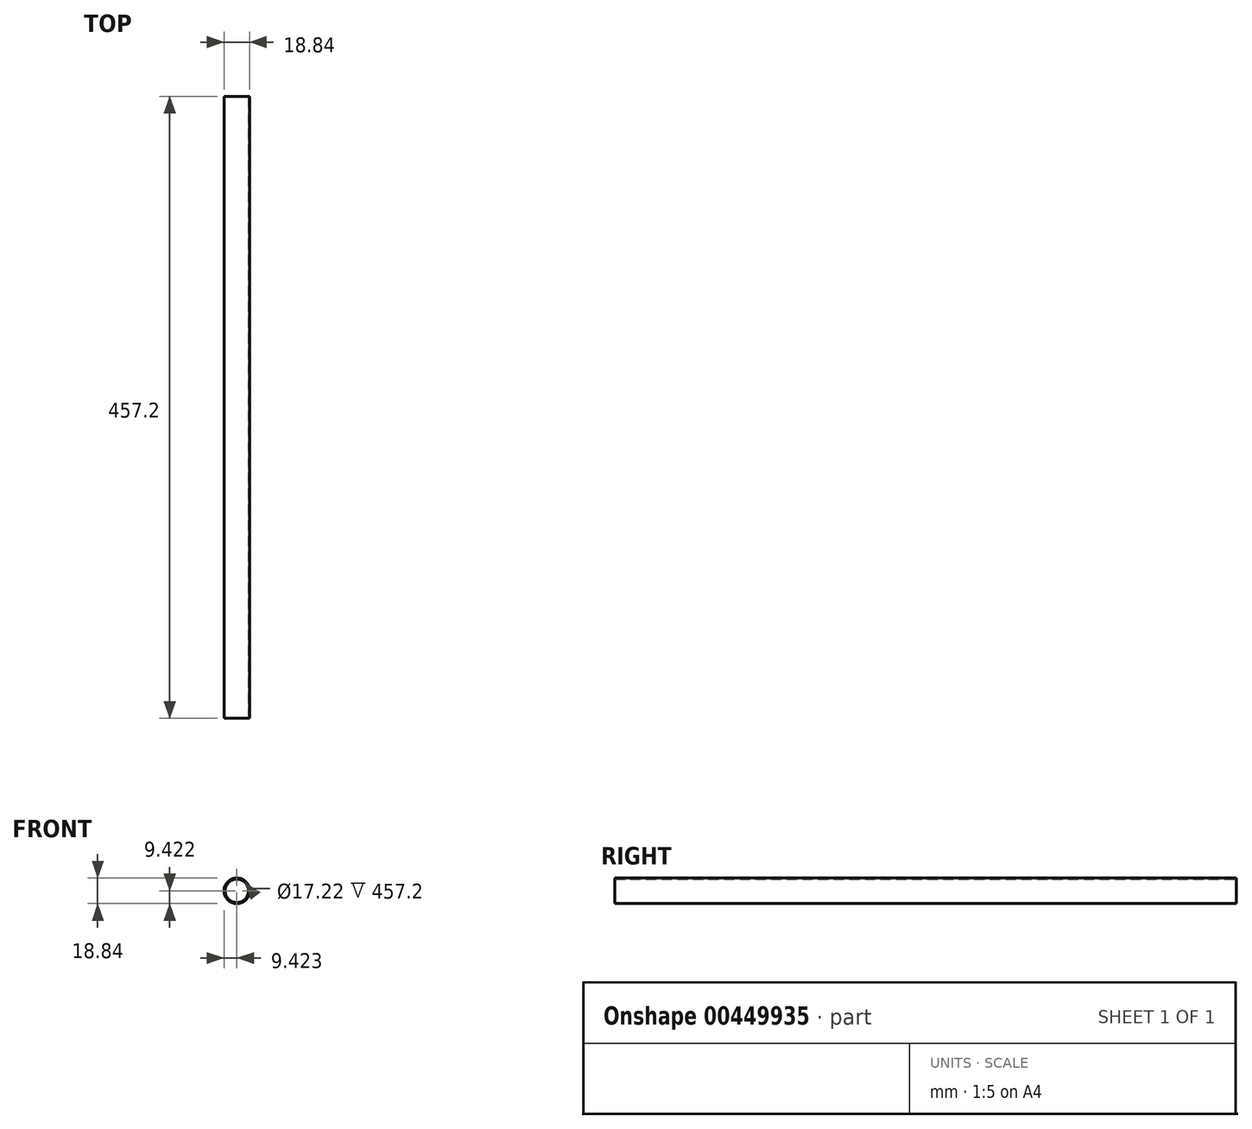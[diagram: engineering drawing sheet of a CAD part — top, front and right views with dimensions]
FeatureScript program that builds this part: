
annotation { "Feature Type Name" : "Feature", "Feature Type Description" : "" }
export const myFeature = defineFeature(function(context is Context, id is Id, definition is map)
    precondition{}
    {
        {
            var Q0;
            Q0=qCreatedBy(makeId("Front.planeOp"),FACE);
            var sketch = newSketch(context, id + "F0", { "sketchPlane" : qUnion([Q0])});
            skCircle(sketch, "E0", {"center": v(-35.1, 35.83) * mm, "radius": 9.42 * mm});
            skCircle(sketch, "E1", {"center": v(-35.1, 35.83) * mm, "radius": 8.61 * mm});
            skSolve(sketch);
        }
        {
            var Q0;
            Q0=makeQuery(id+"F0.imprint","IMPRINT",FACE,{"disambiguationData":[TD([[makeQuery(id+"F0.imprint","IMPRINT",EDGE,{"derivedFrom":sQuery(id+"F0.wireOp",EDGE,"E0")}),1.0]])]});
            extrude(context, id + "F1", {"entities" : qUnion([Q0]), "endBound" : BoundingType.SYMMETRIC, "depth" : 457.2 * mm});
        }
    });
